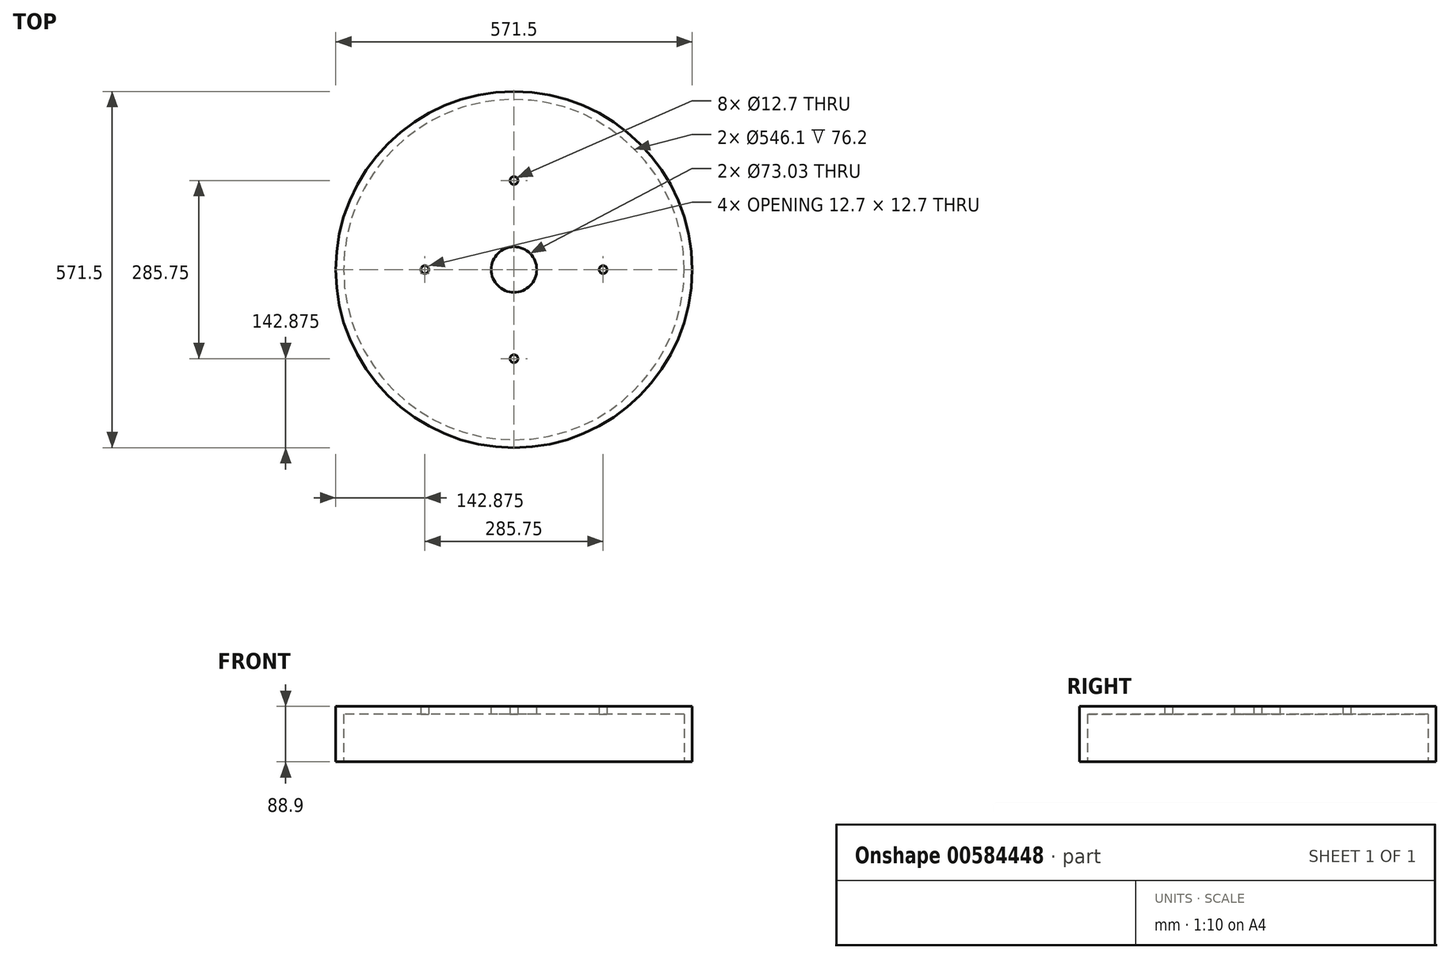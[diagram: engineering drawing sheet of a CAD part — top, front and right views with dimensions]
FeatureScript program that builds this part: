
annotation { "Feature Type Name" : "Feature", "Feature Type Description" : "" }
export const myFeature = defineFeature(function(context is Context, id is Id, definition is map)
    precondition{}
    {
        {
            var Q0;
            Q0=qCreatedBy(makeId("Top.planeOp"),FACE);
            var sketch = newSketch(context, id + "F0", { "sketchPlane" : qUnion([Q0])});
            skCircle(sketch, "E0", {"center": v(0, 0) * mm, "radius": 285.75 * mm});
            skLineSegment(sketch, "E1", {"start": v(-285.75, 0) * mm, "end": v(285.75, 0) * mm, "construction": true});
            skLineSegment(sketch, "E2", {"start": v(285.75, 0) * mm, "end": v(0, 0) * mm, "construction": true});
            skLineSegment(sketch, "E3", {"start": v(-285.75, 0) * mm, "end": v(0, 0) * mm, "construction": true});
            skLineSegment(sketch, "E4", {"start": v(0, 0) * mm, "end": v(0, 285.75) * mm, "construction": true});
            skLineSegment(sketch, "E5", {"start": v(0, 285.75) * mm, "end": v(0, 0) * mm, "construction": true});
            skLineSegment(sketch, "E6", {"start": v(0, 0) * mm, "end": v(0, -285.75) * mm, "construction": true});
            skLineSegment(sketch, "E7", {"start": v(0, -285.75) * mm, "end": v(0, 0) * mm, "construction": true});
            skLineSegment(sketch, "E8.anchor1", {"start": v(0, 0) * mm, "end": v(0, 142.87) * mm, "construction": true});
            skLineSegment(sketch, "E8.anchor2", {"start": v(0, 0) * mm, "end": v(-142.87, 0) * mm, "construction": true});
            skCircle(sketch, "E9", {"center": v(0, 142.87) * mm, "radius": 6.35 * mm});
            skCircle(sketch, "E10.1.0", {"center": v(-142.87, 0) * mm, "radius": 6.35 * mm});
            skCircle(sketch, "E10.2.0", {"center": v(0, -142.87) * mm, "radius": 6.35 * mm});
            skCircle(sketch, "E10.3.0", {"center": v(142.87, 0) * mm, "radius": 6.35 * mm});
            skSolve(sketch);
        }
        {
            var Q0;
            Q0=qSketchRegion(id+"F0",true);
            extrude(context, id + "F1", {"entities" : qUnion([Q0]), "depth" : 88.9 * mm, "offsetDistance" : 25.4 * mm});
        }
        {
            var Q0;
            Q0=makeQuery(id+"F1.opExtrude","CAP_FACE",FACE,{"disambiguationData":[OSD([sQuery(id+"F0.wireOp",EDGE,"E0")])],"isStart":true});
            shell(context, id + "F2", {"entities" : qUnion([Q0]), "thickness" : 12.7 * mm});
        }
        {
            var Q0;
            Q0=makeQuery(id+"F1.opExtrude","CAP_FACE",FACE,{"disambiguationData":[OSD([sQuery(id+"F0.wireOp",EDGE,"E0")])],"isStart":false});
            var sketch = newSketch(context, id + "F3", { "sketchPlane" : qUnion([Q0])});
            skCircle(sketch, "E11", {"center": v(0, 0) * mm, "radius": 36.51 * mm});
            skSolve(sketch);
        }
        {
            var Q0;
            Q0=qSketchRegion(id+"F3",true);
            extrude(context, id + "F4", {"entities" : qUnion([Q0]), "operationType" : NewBodyOperationType.REMOVE, "oppositeDirection" : true, "depth" : 143.82 * mm, "offsetDistance" : 25.4 * mm});
        }
        {
            var Q0;
            {var subQ0=sQuery(id+"F0.wireOp",EDGE,"E10.3.0");var subQ1=sQuery(id+"F0.wireOp",EDGE,"E10.2.0");var subQ2=sQuery(id+"F0.wireOp",EDGE,"E10.1.0");var subQ3=sQuery(id+"F0.wireOp",EDGE,"E9");var subQ4=sQuery(id+"F0.wireOp",EDGE,"E0");Q0=makeQuery(id+"F2.opShell","OFFSET_FACE",FACE,{"disambiguationData":[OSD([subQ4,subQ3,subQ2,subQ1,subQ0]),TDD([makeQuery(id+"F1.opExtrude","CAP_FACE",FACE,{"disambiguationData":[OSD([subQ4,subQ3,subQ2,subQ1,subQ0])],"isStart":false})])]});}
            var sketch = newSketch(context, id + "F5", { "sketchPlane" : qUnion([Q0])});
            skCircle(sketch, "E12", {"center": v(25.25, -5.05) * mm, "radius": 210.5 * mm});
            skSolve(sketch);
        }
        {
            var Q0;
            Q0=qSketchRegion(id+"F5",true);
            extrude(context, id + "F6", {"entities" : qUnion([Q0]), "operationType" : NewBodyOperationType.REMOVE, "depth" : 161.54 * mm, "offsetDistance" : 25.4 * mm});
        }
    });
